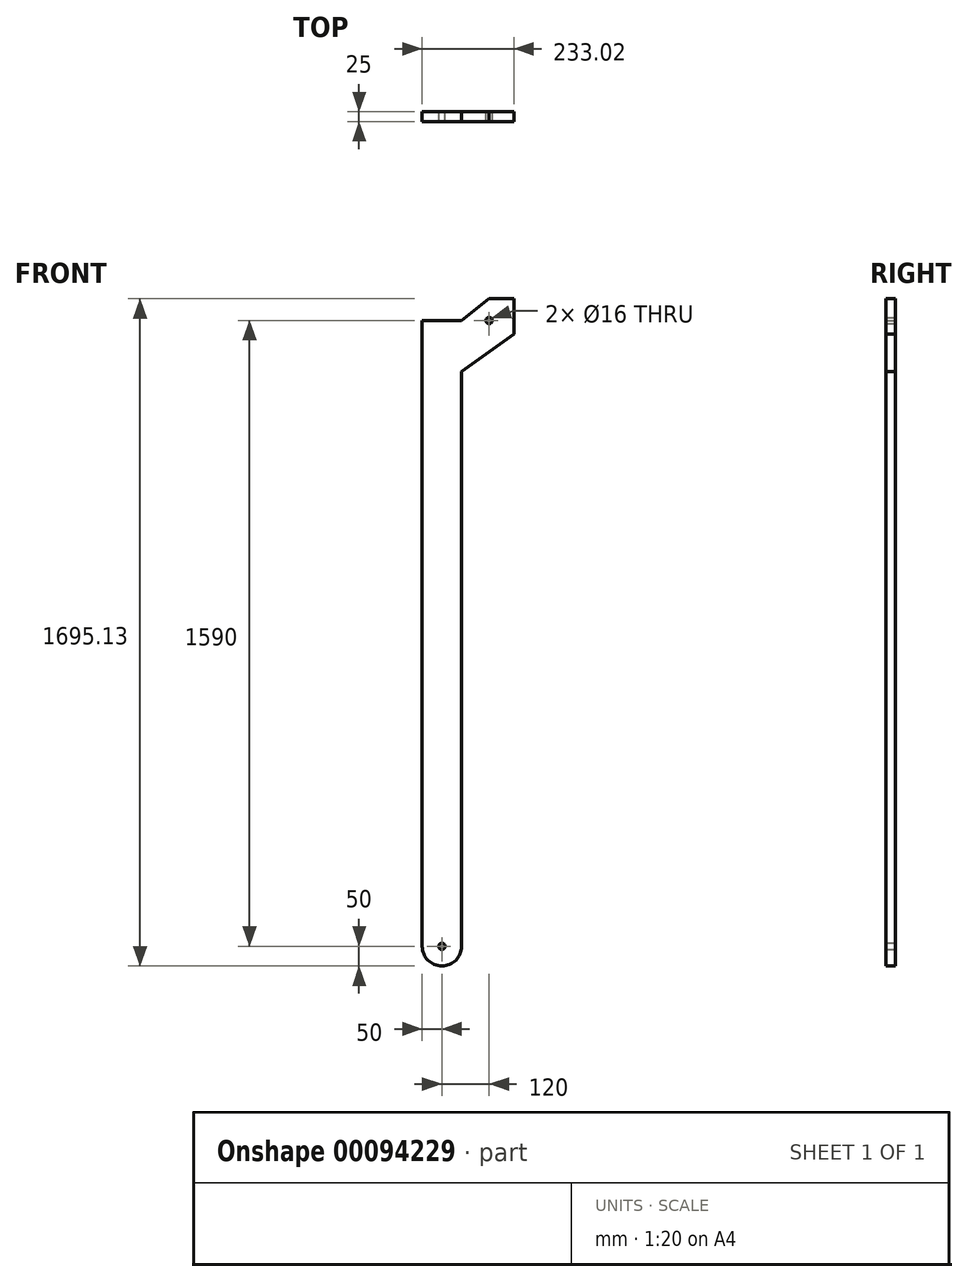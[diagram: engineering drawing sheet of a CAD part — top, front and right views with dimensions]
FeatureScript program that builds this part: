
annotation { "Feature Type Name" : "Feature", "Feature Type Description" : "" }
export const myFeature = defineFeature(function(context is Context, id is Id, definition is map)
    precondition{}
    {
        {
            var Q0;
            Q0=qCreatedBy(makeId("Front.planeOp"),FACE);
            var sketch = newSketch(context, id + "F0", { "sketchPlane" : qUnion([Q0])});
            skLineSegment(sketch, "E0", {"start": v(0, 0) * mm, "end": v(0, 1590) * mm});
            skLineSegment(sketch, "E1", {"start": v(0, 1590) * mm, "end": v(-100, 1590) * mm});
            skLineSegment(sketch, "E2", {"start": v(-100, 1590) * mm, "end": v(-100, 0) * mm});
            skLineSegment(sketch, "E3", {"start": v(-100, 0) * mm, "end": v(0, 0) * mm});
            skCircle(sketch, "E4", {"center": v(70, 1590) * mm, "radius": 8 * mm});
            skCircle(sketch, "E5", {"center": v(-50, 0) * mm, "radius": 8 * mm});
            skCircle(sketch, "E6", {"center": v(-50, 0) * mm, "radius": 50 * mm});
            skLineSegment(sketch, "E7", {"start": v(0, 1590) * mm, "end": v(69.37, 1645.13) * mm});
            skLineSegment(sketch, "E8", {"start": v(69.37, 1645.13) * mm, "end": v(133.02, 1645.13) * mm});
            skLineSegment(sketch, "E9", {"start": v(133.02, 1645.13) * mm, "end": v(133.02, 1556.03) * mm});
            skLineSegment(sketch, "E10", {"start": v(133.02, 1556.03) * mm, "end": v(0, 1460.55) * mm});
            skSolve(sketch);
        }
        {
            var Q0;
            {var subQ5=sQuery(id+"F0.wireOp",EDGE,"E1");Q0=makeQuery(id+"F0.imprint","IMPRINT",FACE,{"disambiguationData":[TD([[makeQuery(id+"F0.imprint","IMPRINT",EDGE,{"derivedFrom":subQ5}),1.0]])]});}
            var Q1;
            Q1=makeQuery(id+"F0.imprint","IMPRINT",FACE,{"disambiguationData":[TD([[makeQuery(id+"F0.imprint","IMPRINT",EDGE,{"derivedFrom":sQuery(id+"F0.wireOp",EDGE,"E4")}),-1.0]])]});
            var Q2;
            {var subQ1=sQuery(id+"F0.wireOp",EDGE,"E3");var subQ3=sQuery(id+"F0.wireOp",EDGE,"E5");var subQ4=makeQuery(id+"F0.imprint","INTERSECT",VERTEX,{"disambiguationData":[OD(0.0)],"derivedFrom":[subQ1,subQ3]});Q2=makeQuery(id+"F0.imprint","IMPRINT",FACE,{"disambiguationData":[TD([[makeQuery(id+"F0.imprint","IMPRINT",EDGE,{"disambiguationData":[TD([[subQ4,-1.0]])],"derivedFrom":subQ3}),-1.0]])]});}
            var Q3;
            {var subQ1=sQuery(id+"F0.wireOp",EDGE,"E3");var subQ3=sQuery(id+"F0.wireOp",EDGE,"E5");var subQ4=makeQuery(id+"F0.imprint","INTERSECT",VERTEX,{"disambiguationData":[OD(0.0)],"derivedFrom":[subQ1,subQ3]});Q3=makeQuery(id+"F0.imprint","IMPRINT",FACE,{"disambiguationData":[TD([[makeQuery(id+"F0.imprint","IMPRINT",EDGE,{"disambiguationData":[TD([[subQ4,1.0]])],"derivedFrom":subQ3}),-1.0]])]});}
            extrude(context, id + "F1", {"entities" : qUnion([Q0, Q1, Q2, Q3]), "depth" : 25 * mm});
        }
    });
